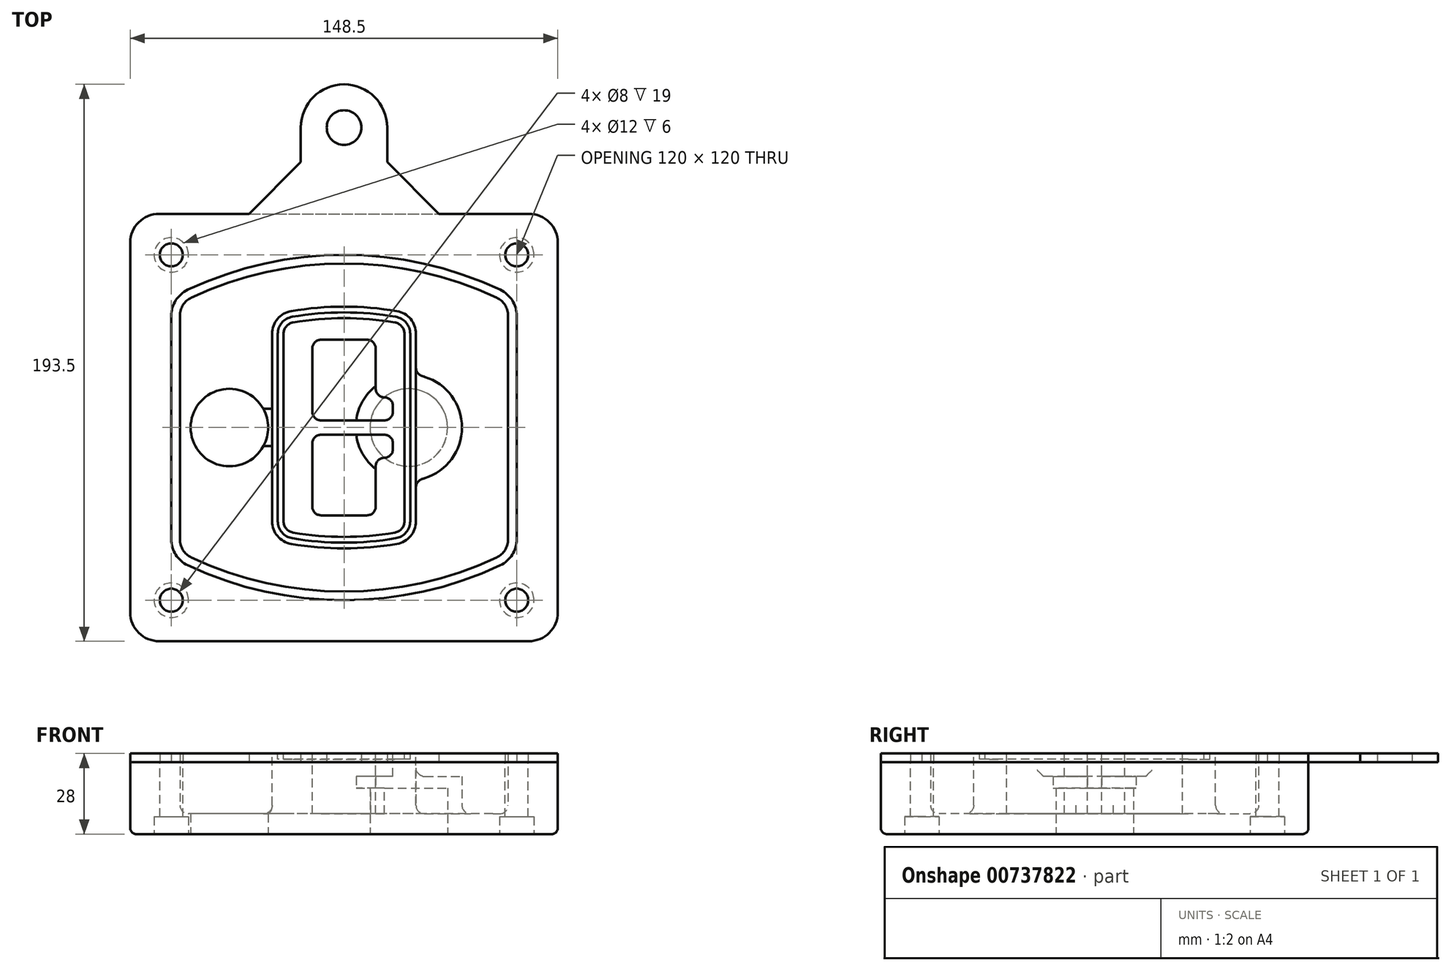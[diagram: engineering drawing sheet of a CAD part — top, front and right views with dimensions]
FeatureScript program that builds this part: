
annotation { "Feature Type Name" : "Feature", "Feature Type Description" : "" }
export const myFeature = defineFeature(function(context is Context, id is Id, definition is map)
    precondition{}
    {
        {
            var Q0;
            Q0=qCreatedBy(makeId("Top.planeOp"),FACE);
            var sketch = newSketch(context, id + "F0", { "sketchPlane" : qUnion([Q0])});
            skPoint(sketch, "E0.rect.middle", {"position": v(0, 0) * mm});
            skLineSegment(sketch, "E1.bottom", {"start": v(-64.25, -74.25) * mm, "end": v(64.25, -74.25) * mm});
            skLineSegment(sketch, "E1.top", {"start": v(-64.25, 74.25) * mm, "end": v(64.25, 74.25) * mm});
            skLineSegment(sketch, "E1.left", {"start": v(-74.25, -64.25) * mm, "end": v(-74.25, 64.25) * mm});
            skLineSegment(sketch, "E1.right", {"start": v(74.25, -64.25) * mm, "end": v(74.25, 64.25) * mm});
            skLineSegment(sketch, "E2", {"start": v(-74.25, 74.25) * mm, "end": v(74.25, -74.25) * mm, "construction": true});
            skLineSegment(sketch, "E3", {"start": v(74.25, 74.25) * mm, "end": v(-74.25, -74.25) * mm, "construction": true});
            skCircle(sketch, "E4", {"center": v(-60, 60) * mm, "radius": 4 * mm});
            skCircle(sketch, "E5", {"center": v(60, 60) * mm, "radius": 4 * mm});
            skCircle(sketch, "E6", {"center": v(60, -60) * mm, "radius": 4 * mm});
            skCircle(sketch, "E7", {"center": v(-60, -60) * mm, "radius": 4 * mm});
            skLineSegment(sketch, "E8", {"start": v(-60, 60) * mm, "end": v(60, 60) * mm, "construction": true});
            skLineSegment(sketch, "E9", {"start": v(60, 60) * mm, "end": v(60, -60) * mm, "construction": true});
            skLineSegment(sketch, "E10", {"start": v(60, -60) * mm, "end": v(-60, -60) * mm, "construction": true});
            skLineSegment(sketch, "E11", {"start": v(-60, -60) * mm, "end": v(-60, 60) * mm, "construction": true});
            skLineSegment(sketch, "E12", {"start": v(-60, 38.83) * mm, "end": v(-60, -38.83) * mm});
            skLineSegment(sketch, "E13", {"start": v(60, 38.83) * mm, "end": v(60, -38.83) * mm});
            skArc(sketch, "E14", {"start": v(54.26, 47.88) * mm, "mid": v(0, 60) * mm, "end": v(-54.26, 47.88) * mm});
            skArc(sketch, "E15", {"start": v(-54.26, -47.88) * mm, "mid": v(0, -60) * mm, "end": v(54.26, -47.88) * mm});
            skLineSegment(sketch, "E16", {"start": v(-60, 0) * mm, "end": v(60, 0) * mm, "construction": true});
            skPoint(sketch, "E17.visualSharp", {"position": v(-60, -45) * mm});
            skArc(sketch, "E17.filletArc", {"start": v(-60, -38.83) * mm, "mid": v(-58.44, -44.2) * mm, "end": v(-54.26, -47.88) * mm});
            skPoint(sketch, "E18.visualSharp", {"position": v(-60, 45) * mm});
            skArc(sketch, "E18.filletArc", {"start": v(-54.26, 47.88) * mm, "mid": v(-58.44, 44.2) * mm, "end": v(-60, 38.83) * mm});
            skPoint(sketch, "E19.visualSharp", {"position": v(60, 45) * mm});
            skArc(sketch, "E19.filletArc", {"start": v(60, 38.83) * mm, "mid": v(58.44, 44.2) * mm, "end": v(54.26, 47.88) * mm});
            skPoint(sketch, "E20.visualSharp", {"position": v(60, -45) * mm});
            skArc(sketch, "E20.filletArc", {"start": v(54.26, -47.88) * mm, "mid": v(58.44, -44.2) * mm, "end": v(60, -38.83) * mm});
            skPoint(sketch, "E21.visualSharp", {"position": v(-74.25, 74.25) * mm});
            skArc(sketch, "E21.filletArc", {"start": v(-64.25, 74.25) * mm, "mid": v(-71.32, 71.32) * mm, "end": v(-74.25, 64.25) * mm});
            skPoint(sketch, "E22.visualSharp", {"position": v(74.25, 74.25) * mm});
            skArc(sketch, "E22.filletArc", {"start": v(74.25, 64.25) * mm, "mid": v(71.32, 71.32) * mm, "end": v(64.25, 74.25) * mm});
            skPoint(sketch, "E23.visualSharp", {"position": v(74.25, -74.25) * mm});
            skArc(sketch, "E23.filletArc", {"start": v(64.25, -74.25) * mm, "mid": v(71.32, -71.32) * mm, "end": v(74.25, -64.25) * mm});
            skPoint(sketch, "E24.visualSharp", {"position": v(-74.25, -74.25) * mm});
            skArc(sketch, "E24.filletArc", {"start": v(-74.25, -64.25) * mm, "mid": v(-71.32, -71.32) * mm, "end": v(-64.25, -74.25) * mm});
            skArc(sketch, "E25.0", {"start": v(57, 38.83) * mm, "mid": v(55.9, 42.58) * mm, "end": v(52.98, 45.17) * mm});
            skLineSegment(sketch, "E25.1", {"start": v(57, 38.83) * mm, "end": v(57, -38.83) * mm});
            skArc(sketch, "E25.2", {"start": v(52.98, -45.17) * mm, "mid": v(55.9, -42.58) * mm, "end": v(57, -38.83) * mm});
            skArc(sketch, "E25.3", {"start": v(-52.98, -45.17) * mm, "mid": v(0, -57) * mm, "end": v(52.98, -45.17) * mm});
            skArc(sketch, "E25.4", {"start": v(-57, -38.83) * mm, "mid": v(-55.9, -42.58) * mm, "end": v(-52.98, -45.17) * mm});
            skArc(sketch, "E25.5", {"start": v(52.98, 45.17) * mm, "mid": v(0, 57) * mm, "end": v(-52.98, 45.17) * mm});
            skLineSegment(sketch, "E25.6", {"start": v(-57, 38.83) * mm, "end": v(-57, -38.83) * mm});
            skArc(sketch, "E25.7", {"start": v(-52.98, 45.17) * mm, "mid": v(-55.9, 42.58) * mm, "end": v(-57, 38.83) * mm});
            skArc(sketch, "E26.0", {"start": v(-55.96, 51.5) * mm, "mid": v(-61.82, 46.33) * mm, "end": v(-64, 38.83) * mm});
            skArc(sketch, "E26.1", {"start": v(55.96, 51.5) * mm, "mid": v(0, 64) * mm, "end": v(-55.96, 51.5) * mm});
            skArc(sketch, "E26.2", {"start": v(64, 38.83) * mm, "mid": v(61.82, 46.33) * mm, "end": v(55.96, 51.5) * mm});
            skLineSegment(sketch, "E26.3", {"start": v(64, 38.83) * mm, "end": v(64, -38.83) * mm});
            skArc(sketch, "E26.4", {"start": v(55.96, -51.5) * mm, "mid": v(61.82, -46.33) * mm, "end": v(64, -38.83) * mm});
            skLineSegment(sketch, "E26.5", {"start": v(-64, 38.83) * mm, "end": v(-64, -38.83) * mm});
            skArc(sketch, "E26.6", {"start": v(-55.96, -51.5) * mm, "mid": v(0, -64) * mm, "end": v(55.96, -51.5) * mm});
            skArc(sketch, "E26.7", {"start": v(-64, -38.83) * mm, "mid": v(-61.82, -46.33) * mm, "end": v(-55.96, -51.5) * mm});
            skSolve(sketch);
        }
        {
            var Q0;
            Q0=makeQuery(id+"F0.imprint","IMPRINT",FACE,{"disambiguationData":[TD([[makeQuery(id+"F0.imprint","IMPRINT",EDGE,{"derivedFrom":sQuery(id+"F0.wireOp",EDGE,"E1.bottom")}),1.0]])]});
            var Q1;
            Q1=makeQuery(id+"F0.imprint","IMPRINT",FACE,{"disambiguationData":[TD([[makeQuery(id+"F0.imprint","IMPRINT",EDGE,{"derivedFrom":sQuery(id+"F0.wireOp",EDGE,"E12")}),1.0]])]});
            var Q2;
            Q2=makeQuery(id+"F0.imprint","IMPRINT",FACE,{"disambiguationData":[TD([[makeQuery(id+"F0.imprint","IMPRINT",EDGE,{"derivedFrom":sQuery(id+"F0.wireOp",EDGE,"E25.0")}),1.0]])]});
            var Q3;
            Q3=makeQuery(id+"F0.imprint","IMPRINT",FACE,{"disambiguationData":[TD([[makeQuery(id+"F0.imprint","IMPRINT",EDGE,{"derivedFrom":sQuery(id+"F0.wireOp",EDGE,"E12")}),-1.0]])]});
            extrude(context, id + "F1", {"entities" : qUnion([Q0, Q1, Q2, Q3]), "oppositeDirection" : true, "depth" : 25 * mm});
        }
        {
            var Q0;
            Q0=makeQuery(id+"F0.imprint","IMPRINT",FACE,{"disambiguationData":[TD([[makeQuery(id+"F0.imprint","IMPRINT",EDGE,{"derivedFrom":sQuery(id+"F0.wireOp",EDGE,"E12")}),1.0]])]});
            extrude(context, id + "F2", {"entities" : qUnion([Q0]), "operationType" : NewBodyOperationType.ADD, "depth" : 3 * mm});
        }
        {
            var Q0;
            Q0=makeQuery(id+"F0.imprint","IMPRINT",FACE,{"disambiguationData":[TD([[makeQuery(id+"F0.imprint","IMPRINT",EDGE,{"derivedFrom":sQuery(id+"F0.wireOp",EDGE,"E25.0")}),1.0]])]});
            extrude(context, id + "F3", {"entities" : qUnion([Q0]), "operationType" : NewBodyOperationType.REMOVE, "oppositeDirection" : true, "depth" : 18 * mm});
        }
        {
            var Q0;
            Q0=makeQuery(id+"F2.opExtrude","CAP_FACE",FACE,{"disambiguationData":[OSD([sQuery(id+"F0.wireOp",EDGE,"E12"),sQuery(id+"F0.wireOp",EDGE,"E13"),sQuery(id+"F0.wireOp",EDGE,"E14"),sQuery(id+"F0.wireOp",EDGE,"E15"),sQuery(id+"F0.wireOp",EDGE,"E17.filletArc"),sQuery(id+"F0.wireOp",EDGE,"E18.filletArc"),sQuery(id+"F0.wireOp",EDGE,"E19.filletArc"),sQuery(id+"F0.wireOp",EDGE,"E20.filletArc"),sQuery(id+"F0.wireOp",EDGE,"E25.0"),sQuery(id+"F0.wireOp",EDGE,"E25.1"),sQuery(id+"F0.wireOp",EDGE,"E25.2"),sQuery(id+"F0.wireOp",EDGE,"E25.3"),sQuery(id+"F0.wireOp",EDGE,"E25.4"),sQuery(id+"F0.wireOp",EDGE,"E25.5"),sQuery(id+"F0.wireOp",EDGE,"E25.6"),sQuery(id+"F0.wireOp",EDGE,"E25.7")])],"isStart":false});
            var sketch = newSketch(context, id + "F4", { "sketchPlane" : qUnion([Q0])});
            skArc(sketch, "E27.0", {"start": v(-18.34, -40.45) * mm, "mid": v(0, -42) * mm, "end": v(18.34, -40.45) * mm});
            skArc(sketch, "E28.0", {"start": v(18.34, 40.45) * mm, "mid": v(0, 42) * mm, "end": v(-18.34, 40.45) * mm});
            skLineSegment(sketch, "E29", {"start": v(-25, 32.57) * mm, "end": v(-25, -32.57) * mm});
            skLineSegment(sketch, "E30", {"start": v(25, 32.57) * mm, "end": v(25, -32.57) * mm});
            skLineSegment(sketch, "E31", {"start": v(-25, 39.1) * mm, "end": v(25, 39.1) * mm, "construction": true});
            skLineSegment(sketch, "E32", {"start": v(-25, -39.1) * mm, "end": v(25, -39.1) * mm, "construction": true});
            skPoint(sketch, "E33.visualSharp", {"position": v(-25, 39.1) * mm});
            skArc(sketch, "E33.filletArc", {"start": v(-18.34, 40.45) * mm, "mid": v(-23.11, 37.73) * mm, "end": v(-25, 32.57) * mm});
            skPoint(sketch, "E34.visualSharp", {"position": v(25, 39.1) * mm});
            skArc(sketch, "E34.filletArc", {"start": v(25, 32.57) * mm, "mid": v(23.11, 37.73) * mm, "end": v(18.34, 40.45) * mm});
            skPoint(sketch, "E35.visualSharp", {"position": v(25, -39.1) * mm});
            skArc(sketch, "E35.filletArc", {"start": v(18.34, -40.45) * mm, "mid": v(23.11, -37.73) * mm, "end": v(25, -32.57) * mm});
            skPoint(sketch, "E36.visualSharp", {"position": v(-25, -39.1) * mm});
            skArc(sketch, "E36.filletArc", {"start": v(-25, -32.57) * mm, "mid": v(-23.11, -37.73) * mm, "end": v(-18.34, -40.45) * mm});
            skArc(sketch, "E37.0", {"start": v(52.98, 45.17) * mm, "mid": v(0, 57) * mm, "end": v(-52.98, 45.17) * mm});
            skArc(sketch, "E37.1", {"start": v(-52.98, 45.17) * mm, "mid": v(-55.9, 42.58) * mm, "end": v(-57, 38.83) * mm});
            skLineSegment(sketch, "E37.2", {"start": v(-57, 38.83) * mm, "end": v(-57, -38.83) * mm});
            skArc(sketch, "E37.3", {"start": v(-57, -38.83) * mm, "mid": v(-55.9, -42.58) * mm, "end": v(-52.98, -45.17) * mm});
            skArc(sketch, "E37.4", {"start": v(-52.98, -45.17) * mm, "mid": v(0, -57) * mm, "end": v(52.98, -45.17) * mm});
            skArc(sketch, "E37.5", {"start": v(52.98, -45.17) * mm, "mid": v(55.9, -42.58) * mm, "end": v(57, -38.83) * mm});
            skLineSegment(sketch, "E37.6", {"start": v(57, 38.83) * mm, "end": v(57, -38.83) * mm});
            skArc(sketch, "E37.7", {"start": v(57, 38.83) * mm, "mid": v(55.9, 42.58) * mm, "end": v(52.98, 45.17) * mm});
            skLineSegment(sketch, "E38.0", {"start": v(23, 32.57) * mm, "end": v(23, -32.57) * mm});
            skArc(sketch, "E38.1", {"start": v(18, -38.48) * mm, "mid": v(21.58, -36.44) * mm, "end": v(23, -32.57) * mm});
            skArc(sketch, "E38.2", {"start": v(-18, -38.48) * mm, "mid": v(0, -40) * mm, "end": v(18, -38.48) * mm});
            skArc(sketch, "E38.3", {"start": v(-23, -32.57) * mm, "mid": v(-21.58, -36.44) * mm, "end": v(-18, -38.48) * mm});
            skLineSegment(sketch, "E38.4", {"start": v(-23, 32.57) * mm, "end": v(-23, -32.57) * mm});
            skArc(sketch, "E38.5", {"start": v(23, 32.57) * mm, "mid": v(21.58, 36.44) * mm, "end": v(18, 38.48) * mm});
            skArc(sketch, "E38.6", {"start": v(-18, 38.48) * mm, "mid": v(-21.58, 36.44) * mm, "end": v(-23, 32.57) * mm});
            skArc(sketch, "E38.7", {"start": v(18, 38.48) * mm, "mid": v(0, 40) * mm, "end": v(-18, 38.48) * mm});
            skArc(sketch, "E39.0", {"start": v(21, 32.57) * mm, "mid": v(20.06, 35.15) * mm, "end": v(17.67, 36.5) * mm});
            skLineSegment(sketch, "E39.1", {"start": v(21, 32.57) * mm, "end": v(21, -32.57) * mm});
            skArc(sketch, "E39.2", {"start": v(17.67, -36.5) * mm, "mid": v(20.06, -35.15) * mm, "end": v(21, -32.57) * mm});
            skArc(sketch, "E39.3", {"start": v(-17.67, -36.5) * mm, "mid": v(0, -38) * mm, "end": v(17.67, -36.5) * mm});
            skArc(sketch, "E39.4", {"start": v(-21, -32.57) * mm, "mid": v(-20.06, -35.15) * mm, "end": v(-17.67, -36.5) * mm});
            skArc(sketch, "E39.5", {"start": v(17.67, 36.5) * mm, "mid": v(0, 38) * mm, "end": v(-17.67, 36.5) * mm});
            skLineSegment(sketch, "E39.6", {"start": v(-21, 32.57) * mm, "end": v(-21, -32.57) * mm});
            skArc(sketch, "E39.7", {"start": v(-17.67, 36.5) * mm, "mid": v(-20.06, 35.15) * mm, "end": v(-21, 32.57) * mm});
            skLineSegment(sketch, "E40", {"start": v(-25, 0) * mm, "end": v(25, 0) * mm, "construction": true});
            skLineSegment(sketch, "E41", {"start": v(-11, 5.5) * mm, "end": v(-11, 27.5) * mm});
            skLineSegment(sketch, "E42", {"start": v(-8, 30.5) * mm, "end": v(8, 30.5) * mm});
            skLineSegment(sketch, "E43", {"start": v(11, 27.5) * mm, "end": v(11, 13.5) * mm});
            skLineSegment(sketch, "E44", {"start": v(14, 10.5) * mm, "end": v(14, 10.5) * mm});
            skLineSegment(sketch, "E45", {"start": v(17, 7.5) * mm, "end": v(17, 5.5) * mm});
            skLineSegment(sketch, "E46", {"start": v(14, 2.5) * mm, "end": v(-8, 2.5) * mm});
            skPoint(sketch, "E47.visualSharp", {"position": v(-11, 30.5) * mm});
            skArc(sketch, "E47.filletArc", {"start": v(-8, 30.5) * mm, "mid": v(-10.12, 29.62) * mm, "end": v(-11, 27.5) * mm});
            skPoint(sketch, "E48.visualSharp", {"position": v(11, 30.5) * mm});
            skArc(sketch, "E48.filletArc", {"start": v(11, 27.5) * mm, "mid": v(10.12, 29.62) * mm, "end": v(8, 30.5) * mm});
            skPoint(sketch, "E49.visualSharp", {"position": v(11, 10.5) * mm});
            skArc(sketch, "E49.filletArc", {"start": v(11, 13.5) * mm, "mid": v(11.88, 11.38) * mm, "end": v(14, 10.5) * mm});
            skPoint(sketch, "E50.visualSharp", {"position": v(17, 10.5) * mm});
            skArc(sketch, "E50.filletArc", {"start": v(17, 7.5) * mm, "mid": v(16.12, 9.62) * mm, "end": v(14, 10.5) * mm});
            skPoint(sketch, "E51.visualSharp", {"position": v(17, 2.5) * mm});
            skArc(sketch, "E51.filletArc", {"start": v(14, 2.5) * mm, "mid": v(16.12, 3.38) * mm, "end": v(17, 5.5) * mm});
            skPoint(sketch, "E52.visualSharp", {"position": v(-11, 2.5) * mm});
            skArc(sketch, "E52.filletArc", {"start": v(-11, 5.5) * mm, "mid": v(-10.12, 3.38) * mm, "end": v(-8, 2.5) * mm});
            skLineSegment(sketch, "E53.0.MirrorCS", {"start": v(14, -2.5) * mm, "end": v(-8, -2.5) * mm});
            skArc(sketch, "E54.0.MirrorCS", {"start": v(-11, -5.5) * mm, "mid": v(-10.12, -3.38) * mm, "end": v(-8, -2.5) * mm});
            skLineSegment(sketch, "E55.0.MirrorCS", {"start": v(-11, -5.5) * mm, "end": v(-11, -27.5) * mm});
            skArc(sketch, "E56.0.MirrorCS", {"start": v(-8, -30.5) * mm, "mid": v(-10.12, -29.62) * mm, "end": v(-11, -27.5) * mm});
            skLineSegment(sketch, "E57.0.MirrorCS", {"start": v(-8, -30.5) * mm, "end": v(8, -30.5) * mm});
            skArc(sketch, "E58.0.MirrorCS", {"start": v(11, -27.5) * mm, "mid": v(10.12, -29.62) * mm, "end": v(8, -30.5) * mm});
            skLineSegment(sketch, "E59.0.MirrorCS", {"start": v(11, -27.5) * mm, "end": v(11, -13.5) * mm});
            skArc(sketch, "E60.0.MirrorCS", {"start": v(11, -13.5) * mm, "mid": v(11.88, -11.38) * mm, "end": v(14, -10.5) * mm});
            skArc(sketch, "E61.0.MirrorCS", {"start": v(17, -7.5) * mm, "mid": v(16.12, -9.62) * mm, "end": v(14, -10.5) * mm});
            skLineSegment(sketch, "E62.0.MirrorCS", {"start": v(17, -7.5) * mm, "end": v(17, -5.5) * mm});
            skArc(sketch, "E63.0.MirrorCS", {"start": v(14, -2.5) * mm, "mid": v(16.12, -3.38) * mm, "end": v(17, -5.5) * mm});
            skSolve(sketch);
        }
        {
            var Q0;
            Q0=makeQuery(id+"F4.imprint","IMPRINT",FACE,{"disambiguationData":[TD([[makeQuery(id+"F4.imprint","IMPRINT",EDGE,{"derivedFrom":sQuery(id+"F4.wireOp",EDGE,"E27.0")}),1.0]])]});
            var Q1;
            Q1=makeQuery(id+"F4.imprint","IMPRINT",FACE,{"disambiguationData":[TD([[makeQuery(id+"F4.imprint","IMPRINT",EDGE,{"derivedFrom":sQuery(id+"F4.wireOp",EDGE,"E38.0")}),-1.0]])]});
            var Q2;
            Q2=makeQuery(id+"F4.imprint","IMPRINT",FACE,{"disambiguationData":[TD([[makeQuery(id+"F4.imprint","IMPRINT",EDGE,{"derivedFrom":sQuery(id+"F4.wireOp",EDGE,"E39.0")}),1.0]])]});
            extrude(context, id + "F5", {"entities" : qUnion([Q0, Q1, Q2]), "operationType" : NewBodyOperationType.ADD, "endBound" : BoundingType.UP_TO_NEXT, "oppositeDirection" : true, "depth" : 25 * mm});
        }
        {
            var Q0;
            Q0=makeQuery(id+"F4.imprint","IMPRINT",FACE,{"disambiguationData":[TD([[makeQuery(id+"F4.imprint","IMPRINT",EDGE,{"derivedFrom":sQuery(id+"F4.wireOp",EDGE,"E38.0")}),-1.0]])]});
            extrude(context, id + "F6", {"entities" : qUnion([Q0]), "operationType" : NewBodyOperationType.REMOVE, "oppositeDirection" : true, "depth" : 2 * mm});
        }
        {
            var Q0;
            Q0=makeQuery(id+"F1.opExtrude","CAP_FACE",FACE,{"disambiguationData":[OSD([sQuery(id+"F0.wireOp",EDGE,"E1.bottom"),sQuery(id+"F0.wireOp",EDGE,"E1.top"),sQuery(id+"F0.wireOp",EDGE,"E1.left"),sQuery(id+"F0.wireOp",EDGE,"E1.right"),sQuery(id+"F0.wireOp",EDGE,"E4"),sQuery(id+"F0.wireOp",EDGE,"E5"),sQuery(id+"F0.wireOp",EDGE,"E6"),sQuery(id+"F0.wireOp",EDGE,"E7"),sQuery(id+"F0.wireOp",EDGE,"E21.filletArc"),sQuery(id+"F0.wireOp",EDGE,"E22.filletArc"),sQuery(id+"F0.wireOp",EDGE,"E23.filletArc"),sQuery(id+"F0.wireOp",EDGE,"E24.filletArc")])],"isStart":false});
            var sketch = newSketch(context, id + "F7", { "sketchPlane" : qUnion([Q0])});
            skCircle(sketch, "E64", {"center": v(22.5, 0) * mm, "radius": 13.47 * mm});
            skCircle(sketch, "E65", {"center": v(-39.81, 0) * mm, "radius": 13.47 * mm});
            skLineSegment(sketch, "E66", {"start": v(74.25, 0) * mm, "end": v(-74.25, 0) * mm});
            skCircle(sketch, "E67", {"center": v(22.5, 0) * mm, "radius": 18.47 * mm});
            skCircle(sketch, "E68", {"center": v(60, -60) * mm, "radius": 6 * mm});
            skCircle(sketch, "E69", {"center": v(-60, -60) * mm, "radius": 6 * mm});
            skCircle(sketch, "E70", {"center": v(-60, 60) * mm, "radius": 6 * mm});
            skCircle(sketch, "E71", {"center": v(60, 60) * mm, "radius": 6 * mm});
            skSolve(sketch);
        }
        {
            var Q0;
            {var subQ1=sQuery(id+"F7.wireOp",EDGE,"E66");var subQ4=sQuery(id+"F7.wireOp",EDGE,"E64");var subQ6=makeQuery(id+"F7.imprint","INTERSECT",VERTEX,{"disambiguationData":[OD(0.0)],"derivedFrom":[subQ4,subQ1]});Q0=makeQuery(id+"F7.imprint","IMPRINT",FACE,{"disambiguationData":[TD([[makeQuery(id+"F7.imprint","IMPRINT",EDGE,{"disambiguationData":[TD([[subQ6,-1.0]])],"derivedFrom":subQ4}),-1.0]])]});}
            var Q1;
            {var subQ0=sQuery(id+"F7.wireOp",EDGE,"E66");var subQ1=sQuery(id+"F7.wireOp",EDGE,"E64");var subQ3=makeQuery(id+"F7.imprint","INTERSECT",VERTEX,{"disambiguationData":[OD(0.0)],"derivedFrom":[subQ1,subQ0]});Q1=makeQuery(id+"F7.imprint","IMPRINT",FACE,{"disambiguationData":[TD([[makeQuery(id+"F7.imprint","IMPRINT",EDGE,{"disambiguationData":[TD([[subQ3,-1.0]])],"derivedFrom":subQ1}),1.0]])]});}
            var Q2;
            {var subQ0=sQuery(id+"F7.wireOp",EDGE,"E66");var subQ1=sQuery(id+"F7.wireOp",EDGE,"E64");var subQ3=makeQuery(id+"F7.imprint","INTERSECT",VERTEX,{"disambiguationData":[OD(0.0)],"derivedFrom":[subQ1,subQ0]});Q2=makeQuery(id+"F7.imprint","IMPRINT",FACE,{"disambiguationData":[TD([[makeQuery(id+"F7.imprint","IMPRINT",EDGE,{"disambiguationData":[TD([[subQ3,1.0]])],"derivedFrom":subQ1}),1.0]])]});}
            var Q3;
            {var subQ1=sQuery(id+"F7.wireOp",EDGE,"E66");var subQ4=sQuery(id+"F7.wireOp",EDGE,"E64");var subQ6=makeQuery(id+"F7.imprint","INTERSECT",VERTEX,{"disambiguationData":[OD(0.0)],"derivedFrom":[subQ4,subQ1]});Q3=makeQuery(id+"F7.imprint","IMPRINT",FACE,{"disambiguationData":[TD([[makeQuery(id+"F7.imprint","IMPRINT",EDGE,{"disambiguationData":[TD([[subQ6,1.0]])],"derivedFrom":subQ4}),-1.0]])]});}
            extrude(context, id + "F8", {"entities" : qUnion([Q0, Q1, Q2, Q3]), "operationType" : NewBodyOperationType.ADD, "oppositeDirection" : true, "depth" : 20 * mm});
        }
        {
            var Q0;
            {var subQ0=sQuery(id+"F7.wireOp",EDGE,"E66");var subQ1=sQuery(id+"F7.wireOp",EDGE,"E64");var subQ3=makeQuery(id+"F7.imprint","INTERSECT",VERTEX,{"disambiguationData":[OD(0.0)],"derivedFrom":[subQ1,subQ0]});Q0=makeQuery(id+"F7.imprint","IMPRINT",FACE,{"disambiguationData":[TD([[makeQuery(id+"F7.imprint","IMPRINT",EDGE,{"disambiguationData":[TD([[subQ3,-1.0]])],"derivedFrom":subQ1}),1.0]])]});}
            var Q1;
            {var subQ0=sQuery(id+"F7.wireOp",EDGE,"E66");var subQ1=sQuery(id+"F7.wireOp",EDGE,"E64");var subQ3=makeQuery(id+"F7.imprint","INTERSECT",VERTEX,{"disambiguationData":[OD(0.0)],"derivedFrom":[subQ1,subQ0]});Q1=makeQuery(id+"F7.imprint","IMPRINT",FACE,{"disambiguationData":[TD([[makeQuery(id+"F7.imprint","IMPRINT",EDGE,{"disambiguationData":[TD([[subQ3,1.0]])],"derivedFrom":subQ1}),1.0]])]});}
            extrude(context, id + "F9", {"entities" : qUnion([Q0, Q1]), "operationType" : NewBodyOperationType.REMOVE, "oppositeDirection" : true, "depth" : 16 * mm});
        }
        {
            var Q0;
            {var subQ0=sQuery(id+"F7.wireOp",EDGE,"E66");var subQ1=sQuery(id+"F7.wireOp",EDGE,"E65");var subQ3=makeQuery(id+"F7.imprint","INTERSECT",VERTEX,{"disambiguationData":[OD(0.0)],"derivedFrom":[subQ1,subQ0]});Q0=makeQuery(id+"F7.imprint","IMPRINT",FACE,{"disambiguationData":[TD([[makeQuery(id+"F7.imprint","IMPRINT",EDGE,{"disambiguationData":[TD([[subQ3,-1.0]])],"derivedFrom":subQ1}),1.0]])]});}
            var Q1;
            {var subQ0=sQuery(id+"F7.wireOp",EDGE,"E66");var subQ1=sQuery(id+"F7.wireOp",EDGE,"E65");var subQ3=makeQuery(id+"F7.imprint","INTERSECT",VERTEX,{"disambiguationData":[OD(0.0)],"derivedFrom":[subQ1,subQ0]});Q1=makeQuery(id+"F7.imprint","IMPRINT",FACE,{"disambiguationData":[TD([[makeQuery(id+"F7.imprint","IMPRINT",EDGE,{"disambiguationData":[TD([[subQ3,1.0]])],"derivedFrom":subQ1}),1.0]])]});}
            extrude(context, id + "F10", {"entities" : qUnion([Q0, Q1]), "operationType" : NewBodyOperationType.REMOVE, "oppositeDirection" : true, "depth" : 25 * mm});
        }
        {
            var Q0;
            Q0=makeQuery(id+"F7.imprint","IMPRINT",FACE,{"disambiguationData":[TD([[makeQuery(id+"F7.imprint","IMPRINT",EDGE,{"derivedFrom":sQuery(id+"F7.wireOp",EDGE,"E68")}),1.0]])]});
            var Q1;
            Q1=makeQuery(id+"F7.imprint","IMPRINT",FACE,{"disambiguationData":[TD([[makeQuery(id+"F7.imprint","IMPRINT",EDGE,{"derivedFrom":makeQuery(id+"F1.opExtrude","CAP_EDGE",EDGE,{"disambiguationData":[OSD([sQuery(id+"F0.wireOp",EDGE,"E5")])],"isStart":false})}),-1.0]])]});
            var Q2;
            Q2=makeQuery(id+"F7.imprint","IMPRINT",FACE,{"disambiguationData":[TD([[makeQuery(id+"F7.imprint","IMPRINT",EDGE,{"derivedFrom":sQuery(id+"F7.wireOp",EDGE,"E69")}),1.0]])]});
            var Q3;
            Q3=makeQuery(id+"F7.imprint","IMPRINT",FACE,{"disambiguationData":[TD([[makeQuery(id+"F7.imprint","IMPRINT",EDGE,{"derivedFrom":makeQuery(id+"F1.opExtrude","CAP_EDGE",EDGE,{"disambiguationData":[OSD([sQuery(id+"F0.wireOp",EDGE,"E4")])],"isStart":false})}),-1.0]])]});
            var Q4;
            Q4=makeQuery(id+"F7.imprint","IMPRINT",FACE,{"disambiguationData":[TD([[makeQuery(id+"F7.imprint","IMPRINT",EDGE,{"derivedFrom":sQuery(id+"F7.wireOp",EDGE,"E70")}),1.0]])]});
            var Q5;
            Q5=makeQuery(id+"F7.imprint","IMPRINT",FACE,{"disambiguationData":[TD([[makeQuery(id+"F7.imprint","IMPRINT",EDGE,{"derivedFrom":makeQuery(id+"F1.opExtrude","CAP_EDGE",EDGE,{"disambiguationData":[OSD([sQuery(id+"F0.wireOp",EDGE,"E7")])],"isStart":false})}),-1.0]])]});
            var Q6;
            Q6=makeQuery(id+"F7.imprint","IMPRINT",FACE,{"disambiguationData":[TD([[makeQuery(id+"F7.imprint","IMPRINT",EDGE,{"derivedFrom":sQuery(id+"F7.wireOp",EDGE,"E71")}),1.0]])]});
            var Q7;
            Q7=makeQuery(id+"F7.imprint","IMPRINT",FACE,{"disambiguationData":[TD([[makeQuery(id+"F7.imprint","IMPRINT",EDGE,{"derivedFrom":makeQuery(id+"F1.opExtrude","CAP_EDGE",EDGE,{"disambiguationData":[OSD([sQuery(id+"F0.wireOp",EDGE,"E6")])],"isStart":false})}),-1.0]])]});
            extrude(context, id + "F11", {"entities" : qUnion([Q0, Q1, Q2, Q3, Q4, Q5, Q6, Q7]), "operationType" : NewBodyOperationType.REMOVE, "oppositeDirection" : true, "depth" : 6 * mm});
        }
        {
            var Q0;
            Q0=makeQuery(id+"F9.boolean.opBoolean","COPY",FACE,{"derivedFrom":makeQuery(id+"F9.opExtrude","CAP_FACE",FACE,{"disambiguationData":[OSD([sQuery(id+"F7.wireOp",EDGE,"E64")])],"isStart":false})});
            var sketch = newSketch(context, id + "F12", { "sketchPlane" : qUnion([Q0])});
            skArc(sketch, "E72.0", {"start": v(11, 14.45) * mm, "mid": v(6.45, 9.13) * mm, "end": v(4.2, 2.5) * mm});
            skArc(sketch, "E72.1", {"start": v(4.2, -2.5) * mm, "mid": v(6.45, -9.13) * mm, "end": v(11, -14.45) * mm});
            skLineSegment(sketch, "E73", {"start": v(4.2, -2.5) * mm, "end": v(14, -2.5) * mm});
            skLineSegment(sketch, "E74.0", {"start": v(14, 2.5) * mm, "end": v(4.2, 2.5) * mm});
            skArc(sketch, "E74.1", {"start": v(14, 2.5) * mm, "mid": v(16.12, 3.38) * mm, "end": v(17, 5.5) * mm});
            skLineSegment(sketch, "E74.2", {"start": v(17, 7.5) * mm, "end": v(17, 5.5) * mm});
            skArc(sketch, "E74.3", {"start": v(17, 7.5) * mm, "mid": v(16.12, 9.62) * mm, "end": v(14, 10.5) * mm});
            skArc(sketch, "E74.4", {"start": v(11, 13.5) * mm, "mid": v(11.88, 11.38) * mm, "end": v(14, 10.5) * mm});
            skLineSegment(sketch, "E74.5", {"start": v(11, 14.45) * mm, "end": v(11, 13.5) * mm});
            skLineSegment(sketch, "E74.7", {"start": v(14, -2.5) * mm, "end": v(4.2, -2.5) * mm});
            skArc(sketch, "E74.8", {"start": v(14, -2.5) * mm, "mid": v(16.12, -3.38) * mm, "end": v(17, -5.5) * mm});
            skLineSegment(sketch, "E74.9", {"start": v(17, -7.5) * mm, "end": v(17, -5.5) * mm});
            skArc(sketch, "E74.10", {"start": v(17, -7.5) * mm, "mid": v(16.12, -9.62) * mm, "end": v(14, -10.5) * mm});
            skArc(sketch, "E74.11", {"start": v(11, -13.5) * mm, "mid": v(11.88, -11.38) * mm, "end": v(14, -10.5) * mm});
            skLineSegment(sketch, "E74.12", {"start": v(11, -14.45) * mm, "end": v(11, -13.5) * mm});
            skPoint(sketch, "E75.orphan", {"position": v(11, -27.5) * mm});
            skPoint(sketch, "E76.orphan", {"position": v(-8, -2.5) * mm});
            skPoint(sketch, "E77.orphan", {"position": v(-8, 2.5) * mm});
            skPoint(sketch, "E78.orphan", {"position": v(11, 27.5) * mm});
            skSolve(sketch);
        }
        {
            var Q0;
            {var subQ7=sQuery(id+"F12.wireOp",EDGE,"E72.0");var subQ14=sQuery(id+"F12.wireOp",EDGE,"E72.1");var subQ16=sQuery(id+"F12.wireOp",EDGE,"E74.1");var subQ18=sQuery(id+"F12.wireOp",EDGE,"E74.8");Q0=qUnion([makeQuery(id+"F12.imprint","IMPRINT",FACE,{"disambiguationData":[TD([[makeQuery(id+"F12.imprint","IMPRINT",EDGE,{"derivedFrom":subQ7}),1.0]])]}),makeQuery(id+"F12.imprint","IMPRINT",FACE,{"disambiguationData":[TD([[makeQuery(id+"F12.imprint","IMPRINT",EDGE,{"derivedFrom":subQ14}),1.0]])]}),makeQuery(id+"F12.imprint","IMPRINT",FACE,{"disambiguationData":[TD([[makeQuery(id+"F12.imprint","IMPRINT",EDGE,{"derivedFrom":subQ16}),1.0]])]}),makeQuery(id+"F12.imprint","IMPRINT",FACE,{"disambiguationData":[TD([[makeQuery(id+"F12.imprint","IMPRINT",EDGE,{"derivedFrom":subQ18}),-1.0]])]})]);}
            var Q1;
            Q1=makeQuery(id+"F5.boolean.opBoolean","SPLIT",FACE,{"disambiguationData":[TD([makeQuery(id+"F5.opExtrude","SWEPT_FACE",FACE,{"disambiguationData":[OSD([sQuery(id+"F4.wireOp",EDGE,"E41")])]})])],"derivedFrom":makeQuery(id+"F3.boolean.opBoolean","COPY",FACE,{"derivedFrom":makeQuery(id+"F3.opExtrude","CAP_FACE",FACE,{"disambiguationData":[OSD([sQuery(id+"F0.wireOp",EDGE,"E25.0"),sQuery(id+"F0.wireOp",EDGE,"E25.1"),sQuery(id+"F0.wireOp",EDGE,"E25.2"),sQuery(id+"F0.wireOp",EDGE,"E25.3"),sQuery(id+"F0.wireOp",EDGE,"E25.4"),sQuery(id+"F0.wireOp",EDGE,"E25.5"),sQuery(id+"F0.wireOp",EDGE,"E25.6"),sQuery(id+"F0.wireOp",EDGE,"E25.7")])],"isStart":false})})});
            extrude(context, id + "F13", {"entities" : qUnion([Q0]), "operationType" : NewBodyOperationType.REMOVE, "endBound" : BoundingType.UP_TO_SURFACE, "endBoundEntityFace" : qUnion([Q1]), "depth" : 25 * mm});
        }
        {
            var Q0;
            Q0=makeQuery(id+"F3.boolean.opBoolean","COPY",EDGE,{"derivedFrom":makeQuery(id+"F3.opExtrude","CAP_EDGE",EDGE,{"disambiguationData":[OSD([sQuery(id+"F0.wireOp",EDGE,"E25.6")])],"isStart":false})});
            var Q1;
            Q1=makeQuery(id+"F8.boolean.opBoolean","INTERSECT",EDGE,{"derivedFrom":[makeQuery(id+"F5.opExtrude","SWEPT_FACE",FACE,{"disambiguationData":[OSD([sQuery(id+"F4.wireOp",EDGE,"E30")])]}),makeQuery(id+"F8.opExtrude","CAP_FACE",FACE,{"disambiguationData":[OSD([sQuery(id+"F7.wireOp",EDGE,"E67")])],"isStart":false})]});
            var Q2;
            Q2=makeQuery(id+"F8.boolean.opBoolean","INTERSECT",EDGE,{"disambiguationData":[OD(1.0)],"derivedFrom":[makeQuery(id+"F5.opExtrude","SWEPT_FACE",FACE,{"disambiguationData":[OSD([sQuery(id+"F4.wireOp",EDGE,"E30")])]}),makeQuery(id+"F8.opExtrude","SWEPT_FACE",FACE,{"disambiguationData":[OSD([sQuery(id+"F7.wireOp",EDGE,"E67")])]})]});
            var Q3;
            {var subQ0=sQuery(id+"F4.wireOp",EDGE,"E30");Q3=makeQuery(id+"F8.boolean.opBoolean","SPLIT",EDGE,{"disambiguationData":[TD([makeQuery(id+"F5.opExtrude","SWEPT_FACE",FACE,{"disambiguationData":[OSD([sQuery(id+"F4.wireOp",EDGE,"E35.filletArc")])]})])],"derivedFrom":makeQuery(id+"F5.opExtrude","CAP_EDGE",EDGE,{"disambiguationData":[OSD([subQ0])],"isStart":false})});}
            var Q4;
            {var subQ0=sQuery(id+"F0.wireOp",EDGE,"E25.7");var subQ1=sQuery(id+"F0.wireOp",EDGE,"E25.1");var subQ2=sQuery(id+"F0.wireOp",EDGE,"E25.6");var subQ3=sQuery(id+"F0.wireOp",EDGE,"E25.5");var subQ4=sQuery(id+"F0.wireOp",EDGE,"E25.4");var subQ5=sQuery(id+"F0.wireOp",EDGE,"E25.0");var subQ6=sQuery(id+"F0.wireOp",EDGE,"E25.2");var subQ7=sQuery(id+"F0.wireOp",EDGE,"E25.3");Q4=makeQuery(id+"F8.boolean.opBoolean","INTERSECT",EDGE,{"derivedFrom":[makeQuery(id+"F5.boolean.opBoolean","SPLIT",FACE,{"disambiguationData":[TD([makeQuery(id+"F2.opExtrude","SWEPT_FACE",FACE,{"disambiguationData":[OSD([subQ5])]})])],"derivedFrom":makeQuery(id+"F3.boolean.opBoolean","COPY",FACE,{"derivedFrom":makeQuery(id+"F3.opExtrude","CAP_FACE",FACE,{"disambiguationData":[OSD([subQ5,subQ1,subQ6,subQ7,subQ4,subQ3,subQ2,subQ0])],"isStart":false})})}),makeQuery(id+"F8.opExtrude","SWEPT_FACE",FACE,{"disambiguationData":[OSD([sQuery(id+"F7.wireOp",EDGE,"E67")])]})]});}
            var Q5;
            Q5=makeQuery(id+"F8.boolean.opBoolean","INTERSECT",EDGE,{"disambiguationData":[OD(0.0)],"derivedFrom":[makeQuery(id+"F5.opExtrude","SWEPT_FACE",FACE,{"disambiguationData":[OSD([sQuery(id+"F4.wireOp",EDGE,"E30")])]}),makeQuery(id+"F8.opExtrude","SWEPT_FACE",FACE,{"disambiguationData":[OSD([sQuery(id+"F7.wireOp",EDGE,"E67")])]})]});
            fillet(context, id + "F14", {"entities" : qUnion([Q0, Q1, Q2, Q3, Q4, Q5]), "radius" : 3 * mm, "tangentPropagation" : true, "allowEdgeOverflow" : false});
        }
        {
            var Q0;
            Q0=makeQuery(id+"F1.opExtrude","CAP_EDGE",EDGE,{"disambiguationData":[OSD([sQuery(id+"F0.wireOp",EDGE,"E1.bottom")])],"isStart":false});
            fillet(context, id + "F15", {"entities" : qUnion([Q0]), "radius" : 2 * mm, "tangentPropagation" : true, "allowEdgeOverflow" : false});
        }
        {
            var Q0;
            {var subQ0=sQuery(id+"F0.wireOp",EDGE,"E21.filletArc");var subQ1=sQuery(id+"F0.wireOp",EDGE,"E7");var subQ2=sQuery(id+"F0.wireOp",EDGE,"E6");var subQ3=sQuery(id+"F0.wireOp",EDGE,"E5");var subQ4=sQuery(id+"F0.wireOp",EDGE,"E4");var subQ5=sQuery(id+"F0.wireOp",EDGE,"E22.filletArc");var subQ6=sQuery(id+"F0.wireOp",EDGE,"E1.bottom");var subQ7=sQuery(id+"F0.wireOp",EDGE,"E1.right");var subQ8=sQuery(id+"F0.wireOp",EDGE,"E1.top");var subQ9=sQuery(id+"F0.wireOp",EDGE,"E1.left");var subQ10=sQuery(id+"F0.wireOp",EDGE,"E23.filletArc");var subQ11=sQuery(id+"F0.wireOp",EDGE,"E24.filletArc");Q0=makeQuery(id+"F2.boolean.opBoolean","SPLIT",FACE,{"disambiguationData":[TD([makeQuery(id+"F1.opExtrude","SWEPT_FACE",FACE,{"disambiguationData":[OSD([subQ6])]})])],"derivedFrom":makeQuery(id+"F1.opExtrude","CAP_FACE",FACE,{"disambiguationData":[OSD([subQ6,subQ8,subQ9,subQ7,subQ4,subQ3,subQ2,subQ1,subQ0,subQ5,subQ10,subQ11])],"isStart":true})});}
            var sketch = newSketch(context, id + "F16", { "sketchPlane" : qUnion([Q0])});
            skLineSegment(sketch, "E79", {"start": v(0, 74.25) * mm, "end": v(0, 104.25) * mm, "construction": true});
            skCircle(sketch, "E80", {"center": v(0, 104.25) * mm, "radius": 6 * mm});
            skLineSegment(sketch, "E81", {"start": v(-33, 74.25) * mm, "end": v(-15, 92.25) * mm});
            skLineSegment(sketch, "E82", {"start": v(-15, 92.25) * mm, "end": v(-15, 104.25) * mm});
            skLineSegment(sketch, "E83", {"start": v(33, 74.25) * mm, "end": v(15, 92.25) * mm});
            skLineSegment(sketch, "E84", {"start": v(15, 92.25) * mm, "end": v(15, 104.25) * mm});
            skArc(sketch, "E85", {"start": v(15, 104.25) * mm, "mid": v(0, 119.25) * mm, "end": v(-15, 104.25) * mm});
            skLineSegment(sketch, "E86", {"start": v(-74.25, 0) * mm, "end": v(74.25, 0) * mm, "construction": true});
            skArc(sketch, "E87.MirrorCS", {"start": v(15, -104.25) * mm, "mid": v(0, -119.25) * mm, "end": v(-15, -104.25) * mm});
            skCircle(sketch, "E88.MirrorC", {"center": v(0, -104.25) * mm, "radius": 6 * mm});
            skLineSegment(sketch, "E89.MirrorCS", {"start": v(-15, -92.25) * mm, "end": v(-15, -104.25) * mm});
            skLineSegment(sketch, "E90.MirrorCS", {"start": v(-33, -74.25) * mm, "end": v(-15, -92.25) * mm});
            skLineSegment(sketch, "E91.MirrorCS", {"start": v(33, -74.25) * mm, "end": v(15, -92.25) * mm});
            skLineSegment(sketch, "E92.MirrorCS", {"start": v(15, -92.25) * mm, "end": v(15, -104.25) * mm});
            skLineSegment(sketch, "E93.MirrorCS", {"start": v(0, -74.25) * mm, "end": v(0, -104.25) * mm, "construction": true});
            skSolve(sketch);
        }
        {
            var Q0;
            Q0=makeQuery(id+"F16.imprint","IMPRINT",FACE,{"disambiguationData":[TD([[makeQuery(id+"F16.imprint","IMPRINT",EDGE,{"derivedFrom":makeQuery(id+"F1.opExtrude","CAP_EDGE",EDGE,{"disambiguationData":[OSD([sQuery(id+"F0.wireOp",EDGE,"E1.left")])],"isStart":true})}),-1.0]])]});
            var Q1;
            Q1=makeQuery(id+"F16.imprint","IMPRINT",FACE,{"disambiguationData":[TD([[makeQuery(id+"F16.imprint","IMPRINT",EDGE,{"derivedFrom":sQuery(id+"F16.wireOp",EDGE,"E80")}),-1.0]])]});
            var Q2;
            Q2=makeQuery(id+"F16.imprint","IMPRINT",FACE,{"disambiguationData":[TD([[makeQuery(id+"F16.imprint","IMPRINT",EDGE,{"derivedFrom":sQuery(id+"F16.wireOp",EDGE,"E87.MirrorCS")}),-1.0]])]});
            var Q3;
            Q3=makeQuery(id+"F2.opExtrude","CAP_FACE",FACE,{"disambiguationData":[OSD([sQuery(id+"F0.wireOp",EDGE,"E12"),sQuery(id+"F0.wireOp",EDGE,"E13"),sQuery(id+"F0.wireOp",EDGE,"E14"),sQuery(id+"F0.wireOp",EDGE,"E15"),sQuery(id+"F0.wireOp",EDGE,"E17.filletArc"),sQuery(id+"F0.wireOp",EDGE,"E18.filletArc"),sQuery(id+"F0.wireOp",EDGE,"E19.filletArc"),sQuery(id+"F0.wireOp",EDGE,"E20.filletArc"),sQuery(id+"F0.wireOp",EDGE,"E25.0"),sQuery(id+"F0.wireOp",EDGE,"E25.1"),sQuery(id+"F0.wireOp",EDGE,"E25.2"),sQuery(id+"F0.wireOp",EDGE,"E25.3"),sQuery(id+"F0.wireOp",EDGE,"E25.4"),sQuery(id+"F0.wireOp",EDGE,"E25.5"),sQuery(id+"F0.wireOp",EDGE,"E25.6"),sQuery(id+"F0.wireOp",EDGE,"E25.7")])],"isStart":false});
            extrude(context, id + "F17", {"entities" : qUnion([Q0, Q1, Q2]), "endBound" : BoundingType.UP_TO_SURFACE, "depth" : 5 * mm, "endBoundEntityFace" : qUnion([Q3]), "offsetDistance" : 25 * mm});
        }
    });
